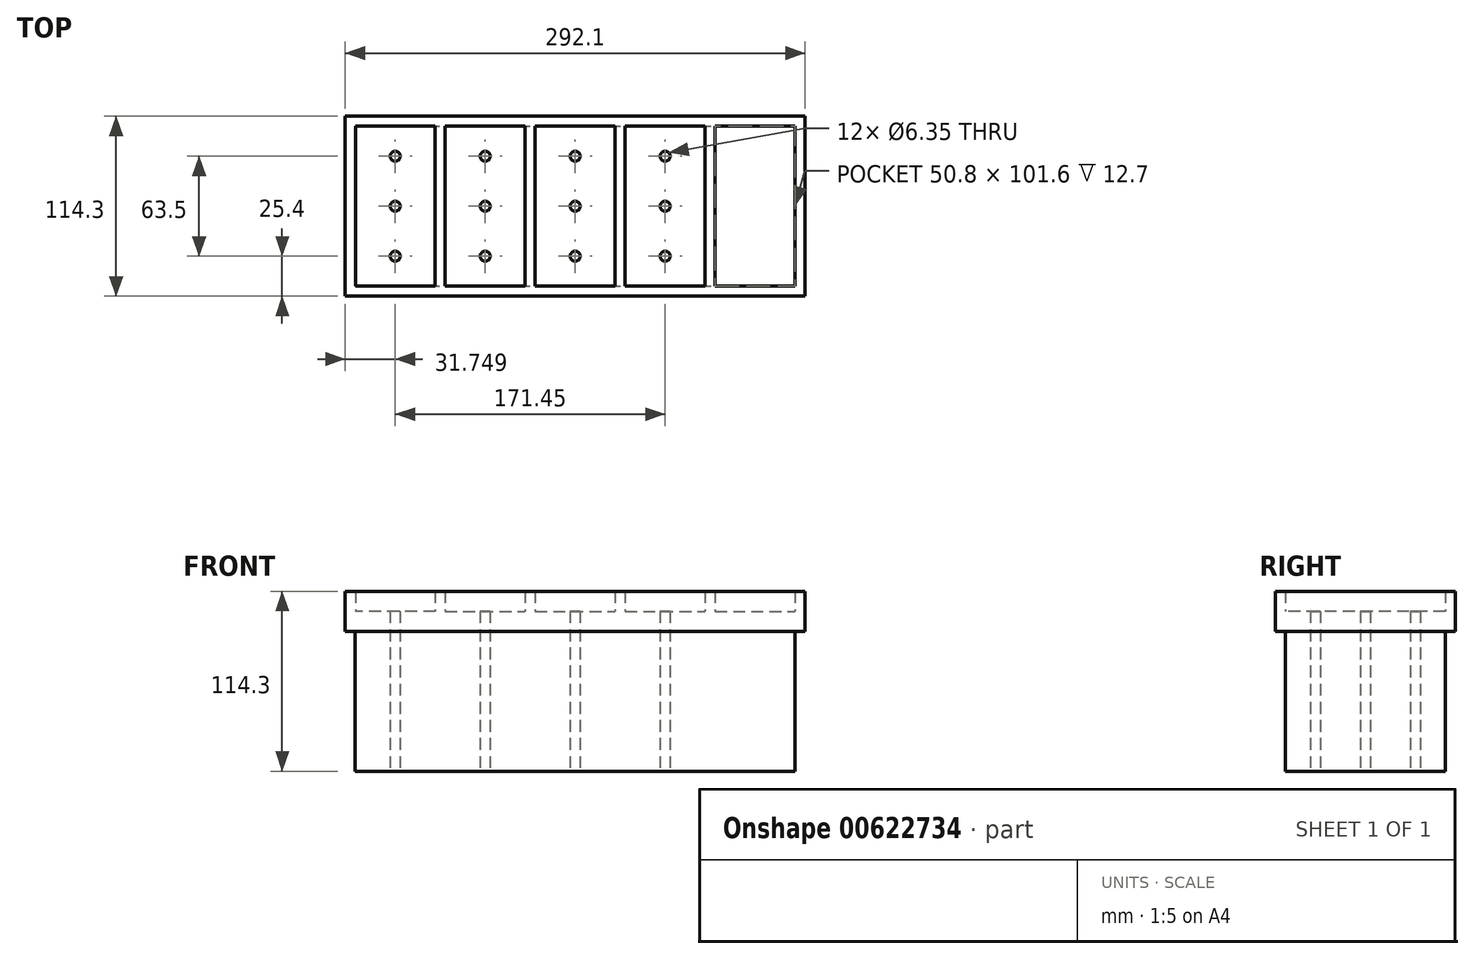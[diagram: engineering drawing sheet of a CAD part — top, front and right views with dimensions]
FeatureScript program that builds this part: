
annotation { "Feature Type Name" : "Feature", "Feature Type Description" : "" }
export const myFeature = defineFeature(function(context is Context, id is Id, definition is map)
    precondition{}
    {
        {
            var Q0;
            Q0=qCreatedBy(makeId("Top.planeOp"),FACE);
            var sketch = newSketch(context, id + "F0", { "sketchPlane" : qUnion([Q0])});
            skLineSegment(sketch, "E0.bottom", {"start": v(-130.36, 52.16) * mm, "end": v(149.04, 52.16) * mm});
            skLineSegment(sketch, "E0.top", {"start": v(-130.36, -49.44) * mm, "end": v(149.04, -49.44) * mm});
            skLineSegment(sketch, "E0.left", {"start": v(-130.36, 52.16) * mm, "end": v(-130.36, -49.44) * mm});
            skLineSegment(sketch, "E0.right", {"start": v(149.04, 52.16) * mm, "end": v(149.04, -49.44) * mm});
            skCircle(sketch, "E1", {"center": v(-104.96, -30.39) * mm, "radius": 3.18 * mm});
            skCircle(sketch, "E2.0.1.0", {"center": v(-104.96, 1.36) * mm, "radius": 3.18 * mm});
            skCircle(sketch, "E2.1.0.0", {"center": v(-47.81, -30.39) * mm, "radius": 3.18 * mm});
            skCircle(sketch, "E2.1.1.0", {"center": v(-47.81, 1.36) * mm, "radius": 3.18 * mm});
            skCircle(sketch, "E2.2.0.0", {"center": v(9.34, -30.39) * mm, "radius": 3.18 * mm});
            skCircle(sketch, "E2.2.1.0", {"center": v(9.34, 1.36) * mm, "radius": 3.18 * mm});
            skCircle(sketch, "E2.3.0.0", {"center": v(66.49, -30.39) * mm, "radius": 3.18 * mm});
            skCircle(sketch, "E2.3.1.0", {"center": v(66.49, 1.36) * mm, "radius": 3.18 * mm});
            skLineSegment(sketch, "E2.direction1", {"start": v(-104.96, -30.39) * mm, "end": v(-47.81, -30.39) * mm, "construction": true});
            skLineSegment(sketch, "E2.direction2", {"start": v(-104.96, -30.39) * mm, "end": v(-104.96, 1.36) * mm, "construction": true});
            skCircle(sketch, "E3.0.0.2", {"center": v(-104.96, 33.11) * mm, "radius": 3.18 * mm});
            skCircle(sketch, "E3.0.1.2", {"center": v(-47.81, 33.11) * mm, "radius": 3.18 * mm});
            skCircle(sketch, "E3.0.2.2", {"center": v(9.34, 33.11) * mm, "radius": 3.18 * mm});
            skCircle(sketch, "E3.0.3.2", {"center": v(66.49, 33.11) * mm, "radius": 3.18 * mm});
            skSolve(sketch);
        }
        {
            var Q0;
            Q0=makeQuery(id+"F0.imprint","IMPRINT",FACE,{"disambiguationData":[TD([[makeQuery(id+"F0.imprint","IMPRINT",EDGE,{"derivedFrom":sQuery(id+"F0.wireOp",EDGE,"E0.bottom")}),-1.0]])]});
            extrude(context, id + "F1", {"entities" : qUnion([Q0]), "depth" : 101.6 * mm, "offsetDistance" : 25.4 * mm});
        }
        {
            var Q0;
            Q0=makeQuery(id+"F1.opExtrude","CAP_FACE",FACE,{"disambiguationData":[OSD([sQuery(id+"F0.wireOp",EDGE,"E0.bottom"),sQuery(id+"F0.wireOp",EDGE,"E0.top"),sQuery(id+"F0.wireOp",EDGE,"E0.left"),sQuery(id+"F0.wireOp",EDGE,"E0.right"),sQuery(id+"F0.wireOp",EDGE,"E1"),sQuery(id+"F0.wireOp",EDGE,"E2.0.1.0"),sQuery(id+"F0.wireOp",EDGE,"E2.1.0.0"),sQuery(id+"F0.wireOp",EDGE,"E2.1.1.0"),sQuery(id+"F0.wireOp",EDGE,"E2.2.0.0"),sQuery(id+"F0.wireOp",EDGE,"E2.2.1.0"),sQuery(id+"F0.wireOp",EDGE,"E2.3.0.0"),sQuery(id+"F0.wireOp",EDGE,"E2.3.1.0")])],"isStart":false});
            var sketch = newSketch(context, id + "F2", { "sketchPlane" : qUnion([Q0])});
            skLineSegment(sketch, "E4.bottom", {"start": v(-79.56, 52.16) * mm, "end": v(-73.21, 52.16) * mm});
            skLineSegment(sketch, "E4.top", {"start": v(-79.56, -49.44) * mm, "end": v(-73.21, -49.44) * mm});
            skLineSegment(sketch, "E4.left", {"start": v(-79.56, 52.16) * mm, "end": v(-79.56, -49.44) * mm});
            skLineSegment(sketch, "E4.right", {"start": v(-73.21, 52.16) * mm, "end": v(-73.21, -49.44) * mm});
            skLineSegment(sketch, "E5.bottom", {"start": v(-16.06, 52.16) * mm, "end": v(-22.41, 52.16) * mm});
            skLineSegment(sketch, "E5.top", {"start": v(-16.06, -49.44) * mm, "end": v(-22.41, -49.44) * mm});
            skLineSegment(sketch, "E5.left", {"start": v(-16.06, 52.16) * mm, "end": v(-16.06, -49.44) * mm});
            skLineSegment(sketch, "E5.right", {"start": v(-22.41, 52.16) * mm, "end": v(-22.41, -49.44) * mm});
            skLineSegment(sketch, "E6.bottom", {"start": v(41.09, 52.16) * mm, "end": v(34.74, 52.16) * mm});
            skLineSegment(sketch, "E6.top", {"start": v(41.09, -49.44) * mm, "end": v(34.74, -49.44) * mm});
            skLineSegment(sketch, "E6.left", {"start": v(41.09, 52.16) * mm, "end": v(41.09, -49.44) * mm});
            skLineSegment(sketch, "E6.right", {"start": v(34.74, 52.16) * mm, "end": v(34.74, -49.44) * mm});
            skLineSegment(sketch, "E7.bottom", {"start": v(98.24, 52.16) * mm, "end": v(91.89, 52.16) * mm});
            skLineSegment(sketch, "E7.top", {"start": v(98.24, -49.44) * mm, "end": v(91.89, -49.44) * mm});
            skLineSegment(sketch, "E7.left", {"start": v(98.24, 52.16) * mm, "end": v(98.24, -49.44) * mm});
            skLineSegment(sketch, "E7.right", {"start": v(91.89, 52.16) * mm, "end": v(91.89, -49.44) * mm});
            skSolve(sketch);
        }
        {
            var Q0;
            Q0=makeQuery(id+"F2.imprint","IMPRINT",FACE,{"disambiguationData":[TD([[makeQuery(id+"F2.imprint","IMPRINT",EDGE,{"derivedFrom":sQuery(id+"F2.wireOp",EDGE,"E4.bottom")}),-1.0]])]});
            var Q1;
            Q1=makeQuery(id+"F2.imprint","IMPRINT",FACE,{"disambiguationData":[TD([[makeQuery(id+"F2.imprint","IMPRINT",EDGE,{"derivedFrom":sQuery(id+"F2.wireOp",EDGE,"E5.bottom")}),-1.0]])]});
            var Q2;
            Q2=makeQuery(id+"F2.imprint","IMPRINT",FACE,{"disambiguationData":[TD([[makeQuery(id+"F2.imprint","IMPRINT",EDGE,{"derivedFrom":sQuery(id+"F2.wireOp",EDGE,"E6.bottom")}),-1.0]])]});
            var Q3;
            Q3=makeQuery(id+"F2.imprint","IMPRINT",FACE,{"disambiguationData":[TD([[makeQuery(id+"F2.imprint","IMPRINT",EDGE,{"derivedFrom":sQuery(id+"F2.wireOp",EDGE,"E7.bottom")}),-1.0]])]});
            extrude(context, id + "F3", {"entities" : qUnion([Q0, Q1, Q2, Q3]), "operationType" : NewBodyOperationType.REMOVE, "oppositeDirection" : true, "depth" : 12.7 * mm, "offsetDistance" : 25.4 * mm});
        }
        {
            var Q0;
            Q0=makeQuery(id+"F3.boolean.opBoolean","COPY",FACE,{"derivedFrom":makeQuery(id+"F3.opExtrude","CAP_FACE",FACE,{"disambiguationData":[OSD([sQuery(id+"F2.wireOp",EDGE,"E4.bottom"),sQuery(id+"F2.wireOp",EDGE,"E4.top"),sQuery(id+"F2.wireOp",EDGE,"E4.left"),sQuery(id+"F2.wireOp",EDGE,"E4.right")])],"isStart":false})});
            var sketch = newSketch(context, id + "F4", { "sketchPlane" : qUnion([Q0])});
            skLineSegment(sketch, "E8.bottom", {"start": v(-136.71, 58.51) * mm, "end": v(155.39, 58.51) * mm});
            skLineSegment(sketch, "E8.top", {"start": v(-136.71, -55.79) * mm, "end": v(155.39, -55.79) * mm});
            skLineSegment(sketch, "E8.left", {"start": v(-136.71, 58.51) * mm, "end": v(-136.71, -55.79) * mm});
            skLineSegment(sketch, "E8.right", {"start": v(155.39, 58.51) * mm, "end": v(155.39, -55.79) * mm});
            skLineSegment(sketch, "E9.bottom", {"start": v(-130.2, 52.11) * mm, "end": v(-79.56, 52.11) * mm});
            skLineSegment(sketch, "E9.top", {"start": v(-130.2, -49.44) * mm, "end": v(-79.56, -49.44) * mm});
            skLineSegment(sketch, "E9.left", {"start": v(-130.2, 52.11) * mm, "end": v(-130.2, -49.44) * mm});
            skLineSegment(sketch, "E9.right", {"start": v(-79.56, 52.11) * mm, "end": v(-79.56, -49.44) * mm});
            skLineSegment(sketch, "E10.bottom", {"start": v(-73.21, 52.16) * mm, "end": v(-22.41, 52.16) * mm});
            skLineSegment(sketch, "E10.top", {"start": v(-73.21, -49.44) * mm, "end": v(-22.41, -49.44) * mm});
            skLineSegment(sketch, "E10.left", {"start": v(-73.21, 52.16) * mm, "end": v(-73.21, -49.44) * mm});
            skLineSegment(sketch, "E10.right", {"start": v(-22.41, 52.16) * mm, "end": v(-22.41, -49.44) * mm});
            skLineSegment(sketch, "E11.bottom", {"start": v(-16.06, 52.16) * mm, "end": v(34.74, 52.16) * mm});
            skLineSegment(sketch, "E11.top", {"start": v(-16.06, -49.44) * mm, "end": v(34.74, -49.44) * mm});
            skLineSegment(sketch, "E11.left", {"start": v(-16.06, 52.16) * mm, "end": v(-16.06, -49.44) * mm});
            skLineSegment(sketch, "E11.right", {"start": v(34.74, 52.16) * mm, "end": v(34.74, -49.44) * mm});
            skLineSegment(sketch, "E12.bottom", {"start": v(41.09, 52.16) * mm, "end": v(91.89, 52.16) * mm});
            skLineSegment(sketch, "E12.top", {"start": v(41.09, -49.44) * mm, "end": v(91.89, -49.44) * mm});
            skLineSegment(sketch, "E12.left", {"start": v(41.09, 52.16) * mm, "end": v(41.09, -49.44) * mm});
            skLineSegment(sketch, "E12.right", {"start": v(91.89, 52.16) * mm, "end": v(91.89, -49.44) * mm});
            skLineSegment(sketch, "E13.bottom", {"start": v(98.24, 52.16) * mm, "end": v(149.04, 52.16) * mm});
            skLineSegment(sketch, "E13.top", {"start": v(98.24, -49.44) * mm, "end": v(149.04, -49.44) * mm});
            skLineSegment(sketch, "E13.left", {"start": v(98.24, 52.16) * mm, "end": v(98.24, -49.44) * mm});
            skLineSegment(sketch, "E13.right", {"start": v(149.04, 52.16) * mm, "end": v(149.04, -49.44) * mm});
            skSolve(sketch);
        }
        {
            var Q0;
            Q0 = qSketchRegion(id + "F4", true);
            extrude(context, id + "F5", {"entities" : qUnion([Q0]), "operationType" : NewBodyOperationType.ADD, "depth" : 25.4 * mm, "offsetDistance" : 25.4 * mm});
        }
    });
